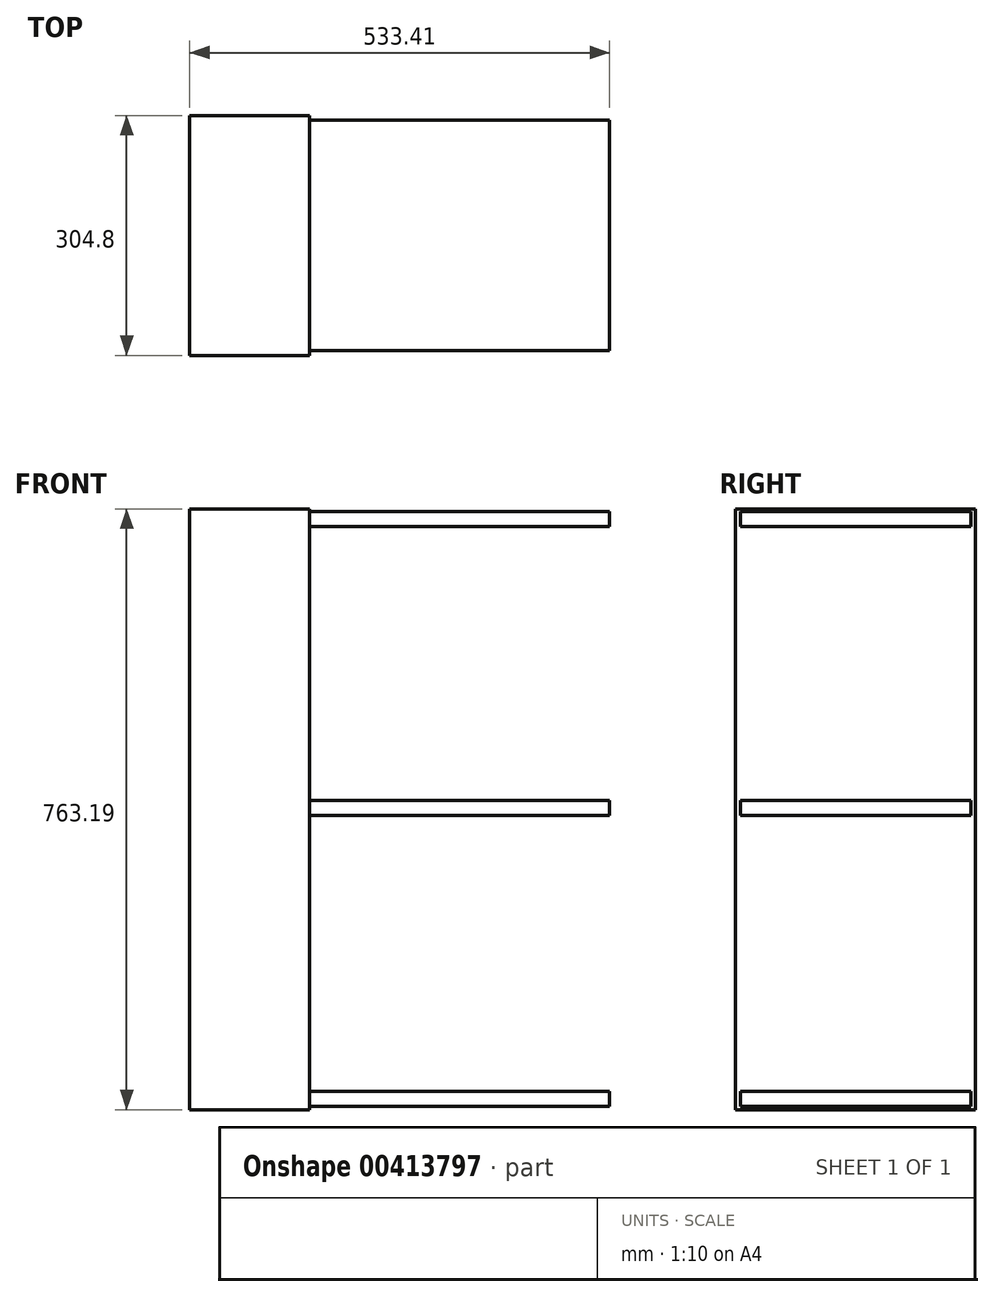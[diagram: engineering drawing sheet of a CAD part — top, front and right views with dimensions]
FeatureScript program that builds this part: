
annotation { "Feature Type Name" : "Feature", "Feature Type Description" : "" }
export const myFeature = defineFeature(function(context is Context, id is Id, definition is map)
    precondition{}
    {
        {
            var Q0;
            Q0=qCreatedBy(makeId("Front.planeOp"),FACE);
            var sketch = newSketch(context, id + "F0", { "sketchPlane" : qUnion([Q0])});
            skLineSegment(sketch, "E0.right", {"start": v(-381, -382.51) * mm, "end": v(-381, 358.45) * mm, "construction": true});
            skPoint(sketch, "E0.middle", {"position": v(0, 0) * mm});
            skLineSegment(sketch, "E1.bottom", {"start": v(-381, -382.51) * mm, "end": v(-533.4, -382.51) * mm});
            skLineSegment(sketch, "E1.top", {"start": v(-381, 380.68) * mm, "end": v(-533.4, 380.68) * mm});
            skLineSegment(sketch, "E1.right", {"start": v(-533.4, -382.51) * mm, "end": v(-533.4, 380.68) * mm});
            skLineSegment(sketch, "E2", {"start": v(0, 377.5) * mm, "end": v(0, 358.45) * mm, "construction": true});
            skLineSegment(sketch, "E3", {"start": v(-381, 380.68) * mm, "end": v(-381, 380.68) * mm});
            skLineSegment(sketch, "E4", {"start": v(0, 358.45) * mm, "end": v(0, 377.5) * mm});
            skLineSegment(sketch, "E5", {"start": v(-381, 13.24) * mm, "end": v(0, 13.24) * mm, "construction": true});
            skLineSegment(sketch, "E6", {"start": v(0, -12.16) * mm, "end": v(0, 13.24) * mm});
            skLineSegment(sketch, "E7", {"start": v(0, 0.54) * mm, "end": v(-381.93, 0.54) * mm, "construction": true});
            skLineSegment(sketch, "E8", {"start": v(-381, -356.25) * mm, "end": v(0, -356.25) * mm, "construction": true});
            skLineSegment(sketch, "E9", {"start": v(0, -378.47) * mm, "end": v(0, -359.42) * mm});
            skLineSegment(sketch, "E10", {"start": v(0, -368.95) * mm, "end": v(-381.94, -369.81) * mm, "construction": true});
            skLineSegment(sketch, "E11.trimOffspring", {"start": v(-381, 13.24) * mm, "end": v(-381, 355.28) * mm});
            skLineSegment(sketch, "E12.trimOffspring", {"start": v(-381, -356.25) * mm, "end": v(-381, -12.16) * mm});
            skLineSegment(sketch, "E13", {"start": v(0, 367.98) * mm, "end": v(-381, 367.98) * mm, "construction": true});
            skLineSegment(sketch, "E14.bottom", {"start": v(0, 377.5) * mm, "end": v(-381, 377.5) * mm});
            skLineSegment(sketch, "E14.top", {"start": v(0, 358.45) * mm, "end": v(-381, 358.45) * mm});
            skLineSegment(sketch, "E14.left", {"start": v(0, 377.5) * mm, "end": v(0, 358.45) * mm});
            skLineSegment(sketch, "E15", {"start": v(-381, 380.68) * mm, "end": v(-381, 377.5) * mm});
            skLineSegment(sketch, "E16", {"start": v(-381, 358.45) * mm, "end": v(-381, 355.28) * mm});
            skLineSegment(sketch, "E17.trimOffspring", {"start": v(-381, 377.5) * mm, "end": v(-381, 380.68) * mm, "construction": true});
            skLineSegment(sketch, "E18.bottom", {"start": v(0.04, 10.07) * mm, "end": v(-381, 10.07) * mm});
            skLineSegment(sketch, "E18.top", {"start": v(0.04, -8.98) * mm, "end": v(-381, -8.98) * mm});
            skLineSegment(sketch, "E19.bottom", {"start": v(0, -359.42) * mm, "end": v(-381, -359.42) * mm});
            skLineSegment(sketch, "E19.top", {"start": v(0, -378.47) * mm, "end": v(-381, -378.47) * mm});
            skLineSegment(sketch, "E20", {"start": v(-381, -12.16) * mm, "end": v(-381, -8.98) * mm});
            skLineSegment(sketch, "E21", {"start": v(-381, 13.24) * mm, "end": v(-381, 10.07) * mm});
            skLineSegment(sketch, "E22", {"start": v(-381, -359.42) * mm, "end": v(-381, -356.25) * mm});
            skLineSegment(sketch, "E23", {"start": v(-381, -382.51) * mm, "end": v(-381, -378.47) * mm});
            skSolve(sketch);
        }
        {
            var Q0;
            Q0 = qSketchRegion(id + "F0", true);
            extrude(context, id + "F1", {"entities" : qUnion([Q0]), "depth" : 152.4 * mm, "hasSecondDirection" : true, "secondDirectionOppositeDirection" : true, "secondDirectionDepth" : 152.4 * mm});
        }
        {
            var Q0;
            Q0=makeQuery(id+"F1.opExtrude","CAP_FACE",FACE,{"disambiguationData":[OSD([sQuery(id+"F0.wireOp",EDGE,"E1.bottom"),sQuery(id+"F0.wireOp",EDGE,"E1.top"),sQuery(id+"F0.wireOp",EDGE,"E1.right"),sQuery(id+"F0.wireOp",EDGE,"E6"),sQuery(id+"F0.wireOp",EDGE,"E9"),sQuery(id+"F0.wireOp",EDGE,"E11.trimOffspring"),sQuery(id+"F0.wireOp",EDGE,"E12.trimOffspring"),sQuery(id+"F0.wireOp",EDGE,"E14.bottom"),sQuery(id+"F0.wireOp",EDGE,"E14.top"),sQuery(id+"F0.wireOp",EDGE,"E14.left"),sQuery(id+"F0.wireOp",EDGE,"E15"),sQuery(id+"F0.wireOp",EDGE,"E16"),sQuery(id+"F0.wireOp",EDGE,"E18.bottom"),sQuery(id+"F0.wireOp",EDGE,"E18.top"),sQuery(id+"F0.wireOp",EDGE,"E19.bottom"),sQuery(id+"F0.wireOp",EDGE,"E19.top"),sQuery(id+"F0.wireOp",EDGE,"E20"),sQuery(id+"F0.wireOp",EDGE,"E21"),sQuery(id+"F0.wireOp",EDGE,"E22"),sQuery(id+"F0.wireOp",EDGE,"E23")])],"isStart":true});
            var sketch = newSketch(context, id + "F2", { "sketchPlane" : qUnion([Q0])});
            skLineSegment(sketch, "E24.0.0", {"start": v(0, -8.98) * mm, "end": v(381, -8.98) * mm});
            skLineSegment(sketch, "E24.0.2", {"start": v(381, -359.42) * mm, "end": v(0, -359.42) * mm});
            skLineSegment(sketch, "E24.0.3", {"start": v(0, -359.42) * mm, "end": v(0, -378.47) * mm});
            skLineSegment(sketch, "E24.0.4", {"start": v(0, -378.47) * mm, "end": v(381, -378.47) * mm});
            skLineSegment(sketch, "E24.0.10", {"start": v(381, 377.5) * mm, "end": v(0, 377.5) * mm});
            skLineSegment(sketch, "E24.0.11", {"start": v(0, 377.5) * mm, "end": v(0, 358.45) * mm});
            skLineSegment(sketch, "E24.0.12", {"start": v(0, 358.45) * mm, "end": v(381, 358.45) * mm});
            skLineSegment(sketch, "E24.0.14", {"start": v(381, 10.07) * mm, "end": v(0, 10.07) * mm});
            skLineSegment(sketch, "E24.0.15", {"start": v(0, 10.07) * mm, "end": v(0, -8.98) * mm});
            skLineSegment(sketch, "E25", {"start": v(381, 377.5) * mm, "end": v(381, 358.45) * mm});
            skLineSegment(sketch, "E26", {"start": v(381, 10.07) * mm, "end": v(381, -8.98) * mm});
            skLineSegment(sketch, "E27", {"start": v(381, -359.42) * mm, "end": v(381, -378.47) * mm});
            skSolve(sketch);
        }
        {
            var Q0;
            Q0=makeQuery(id+"F2.imprint","IMPRINT",FACE,{"disambiguationData":[TD([[makeQuery(id+"F2.imprint","IMPRINT",EDGE,{"derivedFrom":sQuery(id+"F2.wireOp",EDGE,"E24.0.10")}),-1.0]])]});
            var Q1;
            Q1=makeQuery(id+"F2.imprint","IMPRINT",FACE,{"disambiguationData":[TD([[makeQuery(id+"F2.imprint","IMPRINT",EDGE,{"derivedFrom":sQuery(id+"F2.wireOp",EDGE,"E24.0.0")}),1.0]])]});
            var Q2;
            Q2=makeQuery(id+"F2.imprint","IMPRINT",FACE,{"disambiguationData":[TD([[makeQuery(id+"F2.imprint","IMPRINT",EDGE,{"derivedFrom":sQuery(id+"F2.wireOp",EDGE,"E24.0.2")}),-1.0]])]});
            extrude(context, id + "F3", {"entities" : qUnion([Q0, Q1, Q2]), "operationType" : NewBodyOperationType.REMOVE, "oppositeDirection" : true, "depth" : 6.1 * mm});
        }
        {
            var Q0;
            Q0=makeQuery(id+"F1.opExtrude","CAP_FACE",FACE,{"disambiguationData":[OSD([sQuery(id+"F0.wireOp",EDGE,"E1.bottom"),sQuery(id+"F0.wireOp",EDGE,"E1.top"),sQuery(id+"F0.wireOp",EDGE,"E1.right"),sQuery(id+"F0.wireOp",EDGE,"E6"),sQuery(id+"F0.wireOp",EDGE,"E9"),sQuery(id+"F0.wireOp",EDGE,"E11.trimOffspring"),sQuery(id+"F0.wireOp",EDGE,"E12.trimOffspring"),sQuery(id+"F0.wireOp",EDGE,"E14.bottom"),sQuery(id+"F0.wireOp",EDGE,"E14.top"),sQuery(id+"F0.wireOp",EDGE,"E14.left"),sQuery(id+"F0.wireOp",EDGE,"E15"),sQuery(id+"F0.wireOp",EDGE,"E16"),sQuery(id+"F0.wireOp",EDGE,"E18.bottom"),sQuery(id+"F0.wireOp",EDGE,"E18.top"),sQuery(id+"F0.wireOp",EDGE,"E19.bottom"),sQuery(id+"F0.wireOp",EDGE,"E19.top"),sQuery(id+"F0.wireOp",EDGE,"E20"),sQuery(id+"F0.wireOp",EDGE,"E21"),sQuery(id+"F0.wireOp",EDGE,"E22"),sQuery(id+"F0.wireOp",EDGE,"E23")])],"isStart":false});
            var sketch = newSketch(context, id + "F4", { "sketchPlane" : qUnion([Q0])});
            skLineSegment(sketch, "E28.0.0", {"start": v(-381, -8.98) * mm, "end": v(0, -8.98) * mm});
            skLineSegment(sketch, "E28.0.1", {"start": v(0, -8.98) * mm, "end": v(0, 10.07) * mm});
            skLineSegment(sketch, "E28.0.2", {"start": v(0, 10.07) * mm, "end": v(-381, 10.07) * mm});
            skLineSegment(sketch, "E28.0.4", {"start": v(-381, 358.45) * mm, "end": v(0, 358.45) * mm});
            skLineSegment(sketch, "E28.0.5", {"start": v(0, 358.45) * mm, "end": v(0, 377.5) * mm});
            skLineSegment(sketch, "E28.0.6", {"start": v(0, 377.5) * mm, "end": v(-381, 377.5) * mm});
            skLineSegment(sketch, "E28.0.12", {"start": v(-381, -378.47) * mm, "end": v(0, -378.47) * mm});
            skLineSegment(sketch, "E28.0.13", {"start": v(0, -378.47) * mm, "end": v(0, -359.42) * mm});
            skLineSegment(sketch, "E28.0.14", {"start": v(0, -359.42) * mm, "end": v(-381, -359.42) * mm});
            skLineSegment(sketch, "E29", {"start": v(-381, 377.5) * mm, "end": v(-381, 358.45) * mm});
            skLineSegment(sketch, "E30", {"start": v(-381, 10.07) * mm, "end": v(-381, -8.98) * mm});
            skLineSegment(sketch, "E31", {"start": v(-381, -359.42) * mm, "end": v(-381, -378.47) * mm});
            skSolve(sketch);
        }
        {
            var Q0;
            Q0 = qSketchRegion(id + "F4", true);
            extrude(context, id + "F5", {"entities" : qUnion([Q0]), "operationType" : NewBodyOperationType.REMOVE, "oppositeDirection" : true, "depth" : 6.1 * mm});
        }
    });
